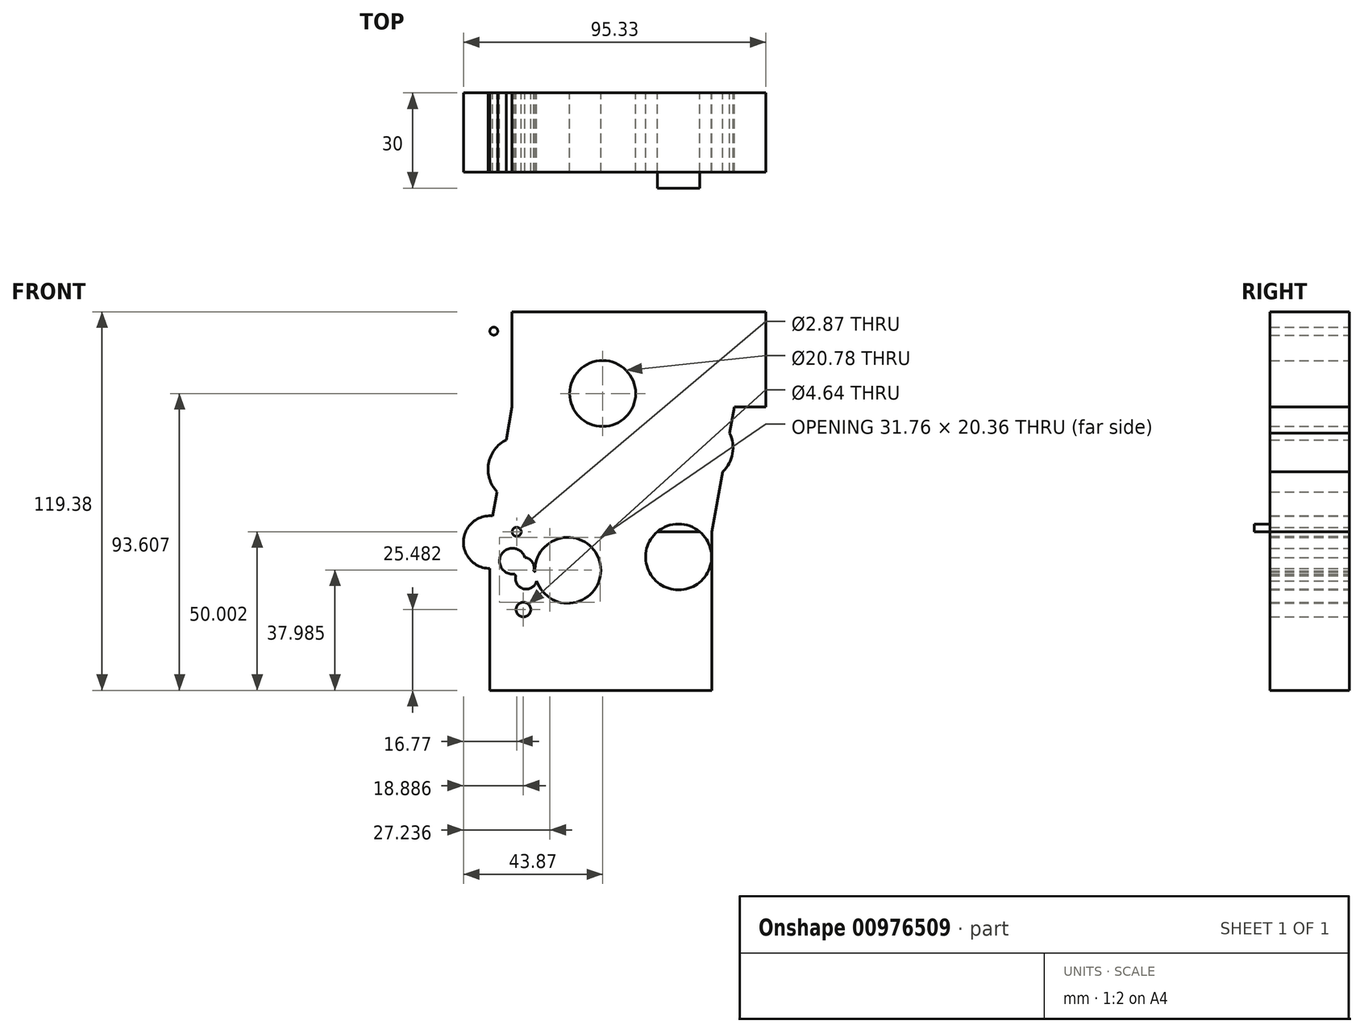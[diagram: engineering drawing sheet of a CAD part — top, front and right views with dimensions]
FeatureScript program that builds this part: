
annotation { "Feature Type Name" : "Feature", "Feature Type Description" : "" }
export const myFeature = defineFeature(function(context is Context, id is Id, definition is map)
    precondition{}
    {
        {
            var Q0;
            Q0=qCreatedBy(makeId("Front.planeOp"),FACE);
            var sketch = newSketch(context, id + "F0", { "sketchPlane" : qUnion([Q0])});
            skLineSegment(sketch, "E0.bottom", {"start": v(-39.15, -13.95) * mm, "end": v(30.85, -13.95) * mm});
            skLineSegment(sketch, "E0.top", {"start": v(-39.15, -63.95) * mm, "end": v(30.85, -63.95) * mm});
            skLineSegment(sketch, "E0.left", {"start": v(-39.15, -13.95) * mm, "end": v(-39.15, -63.95) * mm});
            skLineSegment(sketch, "E0.right", {"start": v(30.85, -13.95) * mm, "end": v(30.85, -63.95) * mm});
            skLineSegment(sketch, "E1", {"start": v(-39.15, -13.95) * mm, "end": v(-32.12, 25.43) * mm});
            skLineSegment(sketch, "E2", {"start": v(37.88, 25.43) * mm, "end": v(30.85, -13.95) * mm});
            skLineSegment(sketch, "E3", {"start": v(-32.12, 25.43) * mm, "end": v(37.88, 25.43) * mm});
            skLineSegment(sketch, "E4.bottom", {"start": v(-32.12, 25.43) * mm, "end": v(47.88, 25.43) * mm});
            skLineSegment(sketch, "E4.top", {"start": v(-32.12, 55.43) * mm, "end": v(47.88, 55.43) * mm});
            skLineSegment(sketch, "E4.left", {"start": v(-32.12, 25.43) * mm, "end": v(-32.12, 55.43) * mm});
            skLineSegment(sketch, "E4.right", {"start": v(47.88, 25.43) * mm, "end": v(47.88, 55.43) * mm});
            skCircle(sketch, "E5", {"center": v(-37.89, 49.33) * mm, "radius": 1.26 * mm});
            skLineSegment(sketch, "E6.direction1", {"start": v(-27.95, 51.72) * mm, "end": v(-52.95, 51.72) * mm, "construction": true});
            skCircle(sketch, "E7", {"center": v(-32.02, -23.21) * mm, "radius": 4.08 * mm});
            skCircle(sketch, "E8", {"center": v(-30.68, -13.95) * mm, "radius": 1.44 * mm});
            skCircle(sketch, "E9", {"center": v(-28.56, -25.38) * mm, "radius": 3.38 * mm});
            skCircle(sketch, "E10", {"center": v(-27.68, -28.65) * mm, "radius": 3.38 * mm});
            skCircle(sketch, "E11", {"center": v(-28.56, -38.47) * mm, "radius": 2.32 * mm});
            skCircle(sketch, "E12", {"center": v(-39.15, -17.2) * mm, "radius": 8.3 * mm});
            skCircle(sketch, "E13", {"center": v(-16.23, -21.84) * mm, "radius": 4.58 * mm});
            skCircle(sketch, "E14", {"center": v(-14.54, -26.1) * mm, "radius": 10.4 * mm});
            skCircle(sketch, "E15.1.0", {"center": v(20.33, -21.89) * mm, "radius": 10.4 * mm});
            skCircle(sketch, "E15.2.0", {"center": v(27.1, 12.57) * mm, "radius": 10.4 * mm});
            skCircle(sketch, "E15.3.0", {"center": v(-3.58, 29.66) * mm, "radius": 10.4 * mm});
            skCircle(sketch, "E15.4.0", {"center": v(-29.31, 5.76) * mm, "radius": 10.4 * mm});
            skPoint(sketch, "E15.center", {"position": v(0, 0) * mm});
            skSolve(sketch);
        }
        {
            var Q0;
            Q0=makeQuery(id+"F0.imprint","IMPRINT",FACE,{"disambiguationData":[TD([[makeQuery(id+"F0.imprint","IMPRINT",EDGE,{"derivedFrom":sQuery(id+"F0.wireOp",EDGE,"E0.bottom")}),1.0]])]});
            extrude(context, id + "F1", {"entities" : qUnion([Q0]), "depth" : 25 * mm, "offsetDistance" : 25 * mm});
        }
        {
            var Q0;
            Q0=makeQuery(id+"F0.imprint","IMPRINT",FACE,{"disambiguationData":[TD([[makeQuery(id+"F0.imprint","IMPRINT",EDGE,{"derivedFrom":sQuery(id+"F0.wireOp",EDGE,"E0.bottom")}),1.0]])]});
            extrude(context, id + "F2", {"entities" : qUnion([Q0]), "operationType" : NewBodyOperationType.ADD, "depth" : 30 * mm, "offsetDistance" : 25 * mm});
        }
        {
            var Q0;
            Q0 = qSketchRegion(id + "F0", true);
            extrude(context, id + "F3", {"entities" : qUnion([Q0]), "operationType" : NewBodyOperationType.ADD, "depth" : 25 * mm, "offsetDistance" : 25 * mm});
        }
    });
